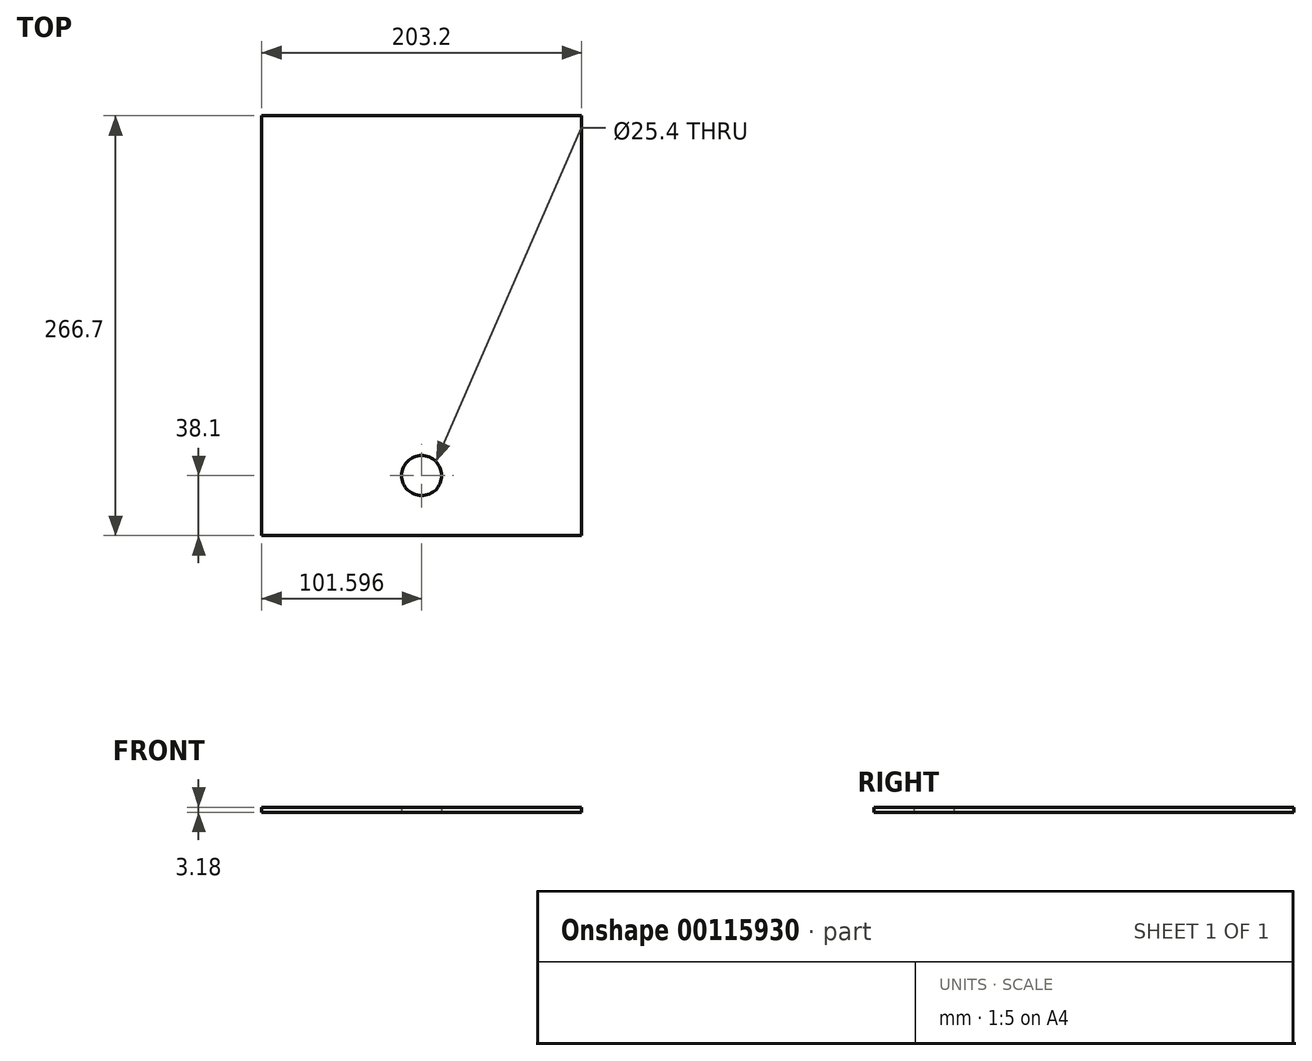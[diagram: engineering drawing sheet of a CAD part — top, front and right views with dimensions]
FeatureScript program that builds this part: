
annotation { "Feature Type Name" : "Feature", "Feature Type Description" : "" }
export const myFeature = defineFeature(function(context is Context, id is Id, definition is map)
    precondition{}
    {
        {
            var Q0;
            Q0=qCreatedBy(makeId("Top.planeOp"),FACE);
            var sketch = newSketch(context, id + "F0", { "sketchPlane" : qUnion([Q0])});
            skLineSegment(sketch, "E0.bottom", {"start": v(-168.3, 139.6) * mm, "end": v(34.9, 139.6) * mm});
            skLineSegment(sketch, "E0.top", {"start": v(-168.3, -127.1) * mm, "end": v(34.9, -127.1) * mm});
            skLineSegment(sketch, "E0.left", {"start": v(-168.3, 139.6) * mm, "end": v(-168.3, -127.1) * mm});
            skLineSegment(sketch, "E0.right", {"start": v(34.9, 139.6) * mm, "end": v(34.9, -127.1) * mm});
            skCircle(sketch, "E1", {"center": v(-66.7, -89) * mm, "radius": 12.7 * mm});
            skPoint(sketch, "E2.bottom.start.orphan", {"position": v(-66.7, -91.12) * mm});
            skSolve(sketch);
        }
        {
            var Q0;
            Q0=makeQuery(id+"F0.imprint","IMPRINT",FACE,{"disambiguationData":[TD([[makeQuery(id+"F0.imprint","IMPRINT",EDGE,{"derivedFrom":sQuery(id+"F0.wireOp",EDGE,"E0.bottom")}),-1.0]])]});
            extrude(context, id + "F1", {"entities" : qUnion([Q0]), "depth" : 3.17 * mm});
        }
    });
